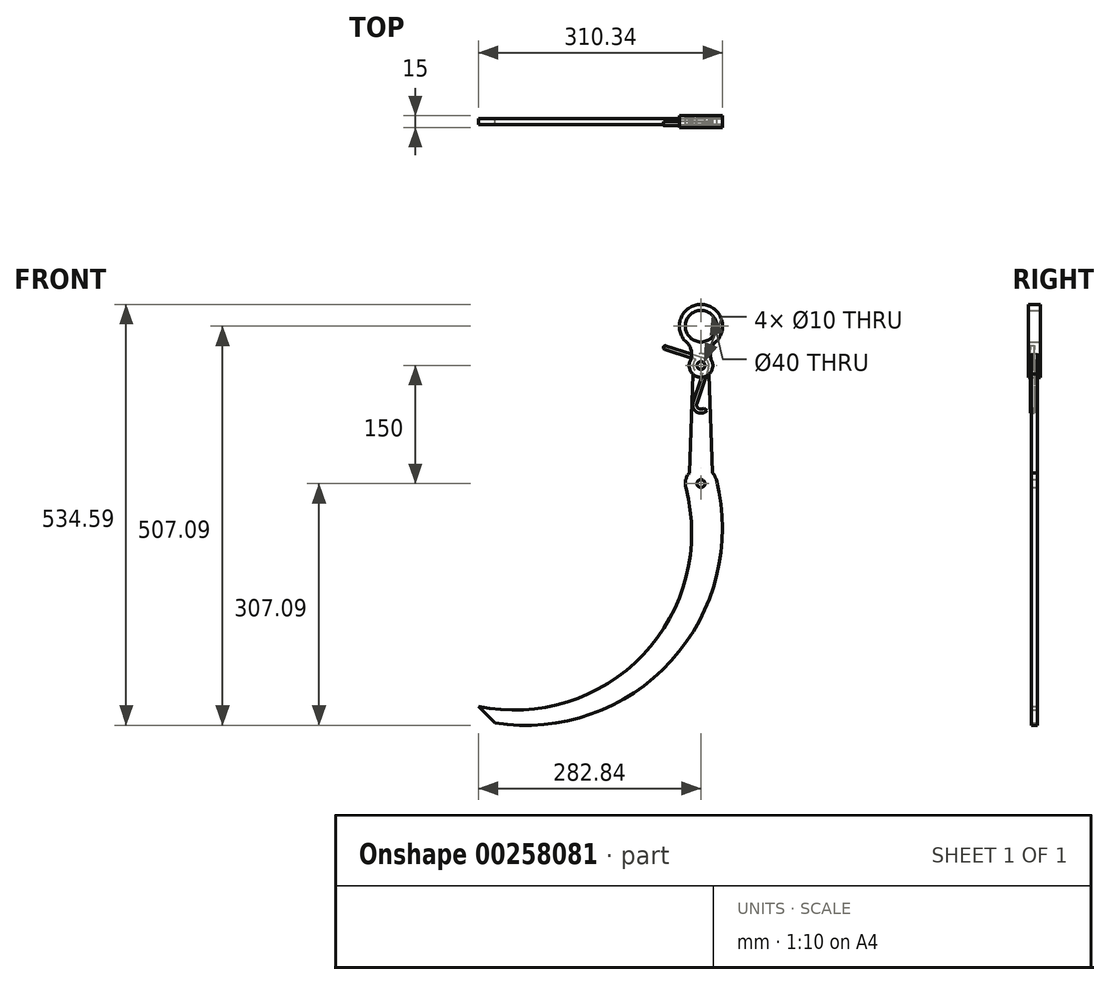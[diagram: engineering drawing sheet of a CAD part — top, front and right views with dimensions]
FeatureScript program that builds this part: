
annotation { "Feature Type Name" : "Feature", "Feature Type Description" : "" }
export const myFeature = defineFeature(function(context is Context, id is Id, definition is map)
    precondition{}
    {
        {
            var Q0;
            Q0=qCreatedBy(makeId("Front.planeOp"),FACE);
            var sketch = newSketch(context, id + "F0", { "sketchPlane" : qUnion([Q0])});
            skCircle(sketch, "E0", {"center": v(0, 0) * mm, "radius": 15 * mm});
            skCircle(sketch, "E1", {"center": v(0, -150) * mm, "radius": 20 * mm});
            skLineSegment(sketch, "E2", {"start": v(0, 0) * mm, "end": v(0, -150) * mm});
            skCircle(sketch, "E3", {"center": v(0, 0) * mm, "radius": 5 * mm});
            skCircle(sketch, "E4", {"center": v(0, -150) * mm, "radius": 5 * mm});
            skLineSegment(sketch, "E5", {"start": v(0, -150) * mm, "end": v(-282.84, -432.84) * mm, "construction": true});
            skArc(sketch, "E6", {"start": v(-282.84, -432.84) * mm, "mid": v(-73.65, -367.45) * mm, "end": v(-19.34, -155.1) * mm});
            skArc(sketch, "E7", {"start": v(-261.63, -454.06) * mm, "mid": v(-37.84, -375.28) * mm, "end": v(19.37, -145.04) * mm});
            skLineSegment(sketch, "E8", {"start": v(-282.84, -432.84) * mm, "end": v(-261.63, -454.06) * mm});
            skLineSegment(sketch, "E9", {"start": v(10, 0) * mm, "end": v(15, -150) * mm});
            skLineSegment(sketch, "E10", {"start": v(15, -150) * mm, "end": v(20, -150) * mm, "construction": true});
            skLineSegment(sketch, "E11.MirrorCS", {"start": v(-10, 0) * mm, "end": v(-15, -150) * mm});
            skLineSegment(sketch, "E12", {"start": v(10, 0) * mm, "end": v(19.96, -148.66) * mm, "construction": true});
            skLineSegment(sketch, "E13.MirrorCS", {"start": v(-10, 0) * mm, "end": v(-19.96, -148.66) * mm, "construction": true});
            skSolve(sketch);
        }
        {
            var Q0;
            Q0=qSketchRegion(id+"F0",true);
            extrude(context, id + "F1", {"entities" : qUnion([Q0]), "depth" : 8 * mm, "symmetric" : true});
        }
        {
            var Q0;
            Q0=qCreatedBy(makeId("Front.planeOp"),FACE);
            var sketch = newSketch(context, id + "F2", { "sketchPlane" : qUnion([Q0])});
            skCircle(sketch, "E14", {"center": v(-236.87, -212.59) * mm, "radius": 225 * mm});
            skCircle(sketch, "E15", {"center": v(-178.43, -276.27) * mm, "radius": 100 * mm});
            skSolve(sketch);
        }
        {
            var Q0;
            Q0=qCreatedBy(makeId("Front.planeOp"),FACE);
            var sketch = newSketch(context, id + "F3", { "sketchPlane" : qUnion([Q0])});
            skCircle(sketch, "E16", {"center": v(0, 0) * mm, "radius": 5 * mm});
            skArc(sketch, "E17", {"start": v(-13.62, 6.3) * mm, "mid": v(0, -15) * mm, "end": v(13.62, 6.3) * mm, "construction": true});
            skCircle(sketch, "E18", {"center": v(0, 50) * mm, "radius": 20 * mm});
            skCircle(sketch, "E19", {"center": v(0, 50) * mm, "radius": 27.5 * mm});
            skArc(sketch, "E20", {"start": v(18.4, 29.56) * mm, "mid": v(12.18, 18.71) * mm, "end": v(13.62, 6.3) * mm});
            skArc(sketch, "E21.MirrorCS", {"start": v(-18.4, 29.56) * mm, "mid": v(-12.18, 18.71) * mm, "end": v(-13.62, 6.3) * mm});
            skArc(sketch, "E22", {"start": v(-13.62, 6.3) * mm, "mid": v(0, -15) * mm, "end": v(13.62, 6.3) * mm});
            skSolve(sketch);
        }
        {
            var Q0;
            Q0 = qSketchRegion(id + "F3", true);
            extrude(context, id + "F4", {"entities" : qUnion([Q0]), "depth" : 15 * mm, "symmetric" : true});
        }
        {
            var Q0;
            Q0=qCreatedBy(makeId("Front.planeOp"),FACE);
            var sketch = newSketch(context, id + "F5", { "sketchPlane" : qUnion([Q0])});
            skCircle(sketch, "E23", {"center": v(0, 0) * mm, "radius": 5 * mm});
            skCircle(sketch, "E24", {"center": v(0, 0) * mm, "radius": 10 * mm});
            skLineSegment(sketch, "E25", {"start": v(3.1, 9.5) * mm, "end": v(-44.44, 25) * mm});
            skLineSegment(sketch, "E26", {"start": v(9.5, -3.1) * mm, "end": v(-5.23, -48.3) * mm});
            skLineSegment(sketch, "E27.0", {"start": v(2.07, -9.78) * mm, "end": v(-9.98, -46.75) * mm});
            skLineSegment(sketch, "E28.0", {"start": v(-6.68, 7.44) * mm, "end": v(-45.99, 20.25) * mm});
            skArc(sketch, "E29", {"start": v(-44.44, 25) * mm, "mid": v(-47.59, 23.4) * mm, "end": v(-45.99, 20.25) * mm});
            skPoint(sketch, "E30.orphan", {"position": v(-9.5, -3.1) * mm});
            skArc(sketch, "E31", {"start": v(-9.98, -46.75) * mm, "mid": v(-5.5, -58.95) * mm, "end": v(7.42, -57.42) * mm});
            skArc(sketch, "E32", {"start": v(-5.23, -48.3) * mm, "mid": v(-2.88, -54.69) * mm, "end": v(3.89, -53.89) * mm});
            skLineSegment(sketch, "E33", {"start": v(3.89, -53.89) * mm, "end": v(7.42, -57.42) * mm});
            skSolve(sketch);
        }
        {
            var Q0;
            Q0 = qSketchRegion(id + "F5", true);
            extrude(context, id + "F6", {"entities" : qUnion([Q0]), "depth" : 5 * mm});
        }
    });
